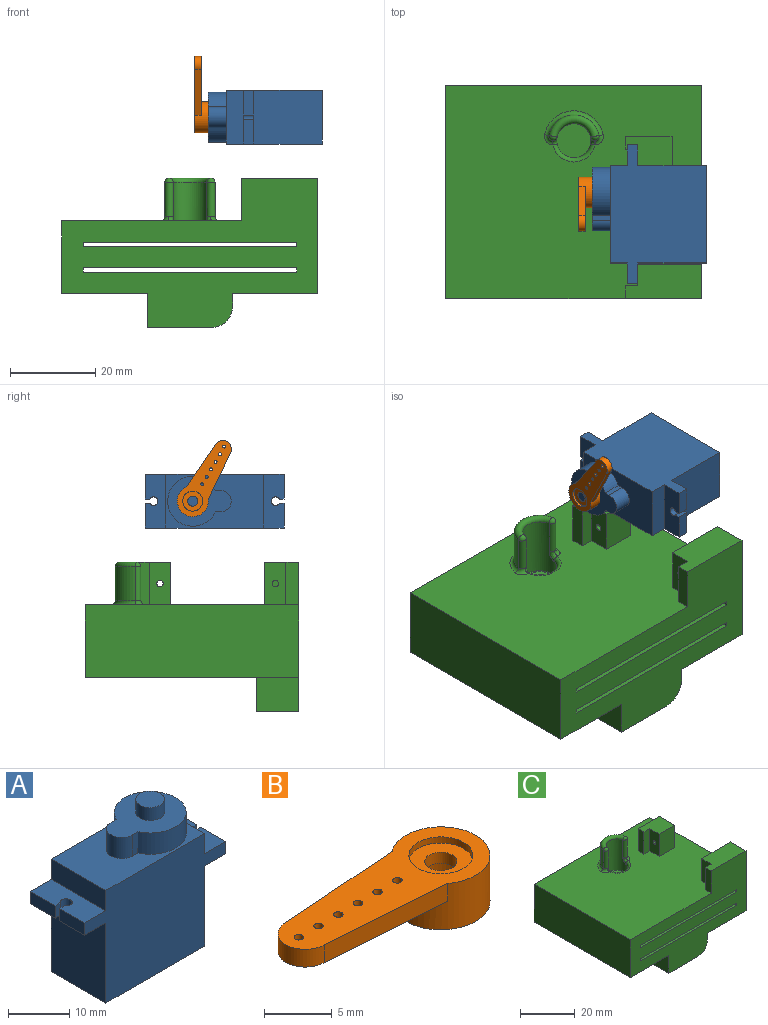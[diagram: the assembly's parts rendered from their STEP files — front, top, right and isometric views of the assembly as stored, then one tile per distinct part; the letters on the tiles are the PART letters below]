
ASSEMBLY  parts=3 mates=2
PART A: 29 faces, bbox 32.6x12.6x29.4 mm
  f0: plane 22.8x12.6mm, normal (0,0,1), area 164.9mm2, adj f3,f4,f5,f6,f22,f23,f24,f25
  f1: plane 16x12.6mm, normal (-1,0,0), area 201.6mm2, adj f4,f6,f7,f21
  f2: plane 16x12.6mm, normal (1,0,0), area 201.6mm2, adj f4,f6,f7,f14
  f3: plane 12.6x4.05mm, normal (1,0,0), area 51mm2, adj f0,f4,f6,f13
  f4: plane 32.6x22.5mm, normal (0,1,0), area 537mm2, adj f0,f1,f2,f3,f5,f7,f12,f13
  f5: plane 12.6x4.05mm, normal (-1,0,0), area 51mm2, adj f0,f4,f6,f20
  f6: plane 32.6x22.5mm, normal (0,-1,0), area 537mm2, adj f0,f1,f2,f3,f5,f7,f8,f13
  f7: plane 22.8x12.6mm, normal (0,0,-1), area 287.3mm2, adj f1,f2,f4,f6
  f8: plane 5.8x2.45mm, normal (1,0,0), area 14.2mm2, adj f6,f9,f13,f14
  f9: plane 2.45x1.13mm, normal (0,1,0), area 2.8mm2, adj f8,f10,f13,f14
  f10: cylinder r=1mm len=2.45mm, axis (0,0,-1), area 12.8mm2, adj f9,f11,f13,f14
  f11: plane 2.45x1.13mm, normal (0,-1,0), area 2.8mm2, adj f10,f12,f13,f14
  f12: plane 5.8x2.45mm, normal (1,0,0), area 14.2mm2, adj f4,f11,f13,f14
  f13: plane 12.6x4.9mm, normal (0,0,1), area 57.6mm2, adj f3,f4,f6,f8,f9,f10,f11,f12
  f14: plane 12.6x4.9mm, normal (0,0,-1), area 57.6mm2, adj f2,f4,f6,f8,f9,f10,f11,f12
  f15: plane 5.8x2.45mm, normal (-1,0,0), area 14.2mm2, adj f4,f16,f20,f21
  f16: plane 2.45x1.13mm, normal (0,-1,0), area 2.8mm2, adj f15,f17,f20,f21
  f17: cylinder r=1mm len=2.45mm, axis (0,0,-1), area 12.8mm2, adj f16,f18,f20,f21
  f18: plane 2.45x1.13mm, normal (0,1,0), area 2.8mm2, adj f17,f19,f20,f21
  f19: plane 5.8x2.45mm, normal (-1,0,0), area 14.2mm2, adj f6,f18,f20,f21
  f20: plane 12.6x4.9mm, normal (0,0,1), area 57.6mm2, adj f4,f5,f6,f15,f16,f17,f18,f19
  f21: plane 12.6x4.9mm, normal (0,0,-1), area 57.6mm2, adj f1,f4,f6,f15,f16,f17,f18,f19
  f22: plane 4.25x1.21mm, normal (0,1,0), area 5.1mm2, adj f0,f23,f25,f26
  f23: cylinder r=2.5mm len=5mm, axis (0,0,-1), area 33.4mm2, adj f0,f22,f24,f26
  f24: plane 4.25x1.21mm, normal (0,-1,0), area 5.1mm2, adj f0,f23,f25,f26
  f25: cylinder r=5.88mm len=11.75mm, axis (0,0,-1), area 134.9mm2, adj f0,f22,f24,f26
  f26: plane 14.9x11.75mm, normal (0,0,1), area 105.1mm2, adj f22,f23,f24,f25,f27
  f27: cylinder r=2.35mm len=4.7mm, axis (0,0,-1), area 38.4mm2, adj f26,f28
  f28: plane 4.7x4.7mm, normal (0,0,1), area 17.3mm2, adj f27
PART B: 18 faces, bbox 19.8x7.3x4.2 mm
  f0: cylinder r=2.35mm len=4.7mm, axis (0,0,-1), area 38.4mm2, adj f13,f15
  f1: cylinder r=3.62mm len=7.25mm, axis (0,0,-1), area 83.8mm2, adj f2,f9,f12,f13,f17
  f2: plane 11.95x1.6mm, normal (-0.08,1,0), area 19.2mm2, adj f1,f3,f12,f17
  f3: cylinder r=2mm len=4mm, axis (0,0,-1), area 10.1mm2, adj f2,f9,f12,f17
  f4: cylinder r=0.35mm len=1.6mm, axis (0,0,-1), area 3.5mm2, adj f12,f17
  f5: cylinder r=0.35mm len=1.6mm, axis (0,0,-1), area 3.5mm2, adj f12,f17
  f6: cylinder r=0.35mm len=1.6mm, axis (0,0,-1), area 3.5mm2, adj f12,f17
  f7: cylinder r=0.35mm len=1.6mm, axis (0,0,-1), area 3.5mm2, adj f12,f17
  f8: cylinder r=0.35mm len=1.6mm, axis (0,0,-1), area 3.5mm2, adj f12,f17
  f9: plane 11.95x1.6mm, normal (-0.08,-1,0), area 19.2mm2, adj f1,f3,f12,f17
  f10: cylinder r=2.35mm len=4.7mm, axis (0,0,-1), area 8.1mm2, adj f12,f14
  f11: cylinder r=0.35mm len=1.6mm, axis (0,0,-1), area 3.5mm2, adj f12,f17
  f12: plane 19.75x7.25mm, normal (0,0,1), area 80.6mm2, adj f1,f2,f3,f4,f5,f6,f7,f8
  f13: plane 7.25x7.25mm, normal (0,0,-1), area 23.9mm2, adj f0,f1
  f14: plane 4.7x4.7mm, normal (0,0,1), area 13mm2, adj f10,f16
  f15: plane 4.7x4.7mm, normal (0,0,-1), area 13mm2, adj f0,f16
  f16: cylinder r=1.18mm len=2.35mm, axis (0,0,-1), area 7.4mm2, adj f14,f15
  f17: plane 13.95x5.8mm, normal (0,0,-1), area 56.7mm2, adj f1,f2,f3,f4,f5,f6,f7,f8
PART C: 52 faces, bbox 60x50x35 mm
  f0: cylinder r=4mm len=14mm, axis (0,0,1), area 211.5mm2, adj f26,f34,f39,f40,f44,f45,f46
  f1: plane 60x17mm, normal (0,1,0), area 920mm2, adj f4,f5,f6,f7,f22,f23,f24,f25
  f2: plane 60x35mm, normal (0,-1,0), area 1254.6mm2, adj f4,f5,f6,f7,f11,f12,f22,f23
  f3: plane 10x8mm, normal (0,-1,0), area 80mm2, adj f4,f16,f17,f18
  f4: plane 60x50mm, normal (0,0,1), area 2679.8mm2, adj f1,f2,f3,f5,f6,f8,f9,f10
  f5: plane 50x27mm, normal (1,0,0), area 930mm2, adj f1,f2,f4,f7,f8,f12
  f6: plane 50x17mm, normal (-1,0,0), area 850mm2, adj f1,f2,f4,f7
  f7: plane 60x50mm, normal (0,0,-1), area 2800mm2, adj f1,f2,f5,f6,f47,f48,f49
  f8: plane 15x10mm, normal (0,1,0), area 150mm2, adj f4,f5,f9,f12
  f9: plane 10x5mm, normal (-1,0,0), area 48.2mm2, adj f4,f8,f10,f12,f20
  f10: plane 10x3mm, normal (0,1,0), area 30mm2, adj f4,f9,f11,f12
  f11: plane 10x3mm, normal (-1,0,0), area 30mm2, adj f2,f4,f10,f12
  f12: plane 18x8mm, normal (0,0,1), area 129mm2, adj f2,f5,f8,f9,f10,f11
  f13: plane 11x10mm, normal (0,1,0), area 110mm2, adj f4,f14,f17,f18
  f14: plane 10x3mm, normal (-1,0,0), area 30mm2, adj f4,f13,f15,f17
  f15: plane 10x3mm, normal (0,-1,0), area 30mm2, adj f4,f14,f16,f17
  f16: plane 10x5mm, normal (-1,0,0), area 48.2mm2, adj f3,f4,f15,f17,f19
  f17: plane 11x8mm, normal (0,0,1), area 73mm2, adj f3,f13,f14,f15,f16,f18
  f18: plane 10x8mm, normal (1,0,0), area 78.2mm2, adj f3,f4,f13,f17,f19
  f19: cylinder r=0.75mm len=8mm, axis (-1,0,0), area 37.7mm2, adj f16,f18
  f20: cylinder r=0.75mm len=8mm, axis (-1,0,0), area 37.7mm2, adj f9,f21
  f21: plane 1.5x1.5mm, normal (-1,0,0), area 1.8mm2, adj f20
  f22: plane 50x50mm, normal (0,0,-1), area 2500mm2, adj f1,f2,f23,f25
  f23: plane 50x1mm, normal (-1,0,0), area 50mm2, adj f1,f2,f22,f24
  f24: plane 50x50mm, normal (0,0,1), area 2500mm2, adj f1,f2,f23,f25
  f25: plane 50x1mm, normal (1,0,0), area 50mm2, adj f1,f2,f22,f24
  f26: plane 50x50mm, normal (0,0,-1), area 2449.7mm2, adj f0,f1,f2,f27,f29
  f27: plane 50x1mm, normal (-1,0,0), area 50mm2, adj f1,f2,f26,f28
  f28: plane 50x50mm, normal (0,0,1), area 2421.5mm2, adj f1,f2,f27,f29,f32
  f29: plane 50x1mm, normal (1,0,0), area 50mm2, adj f1,f2,f26,f28
  f30: plane 8x8mm, normal (0,0,1), area 50.3mm2, adj f31
  f31: cylinder r=4mm len=8mm, axis (0,0,1), area 50.3mm2, adj f30,f32
  f32: torus R=5mm, axis (0,0,-1), area 43.1mm2, adj f28,f31
  f33: cylinder r=6mm len=11.76mm, axis (0,0,-1), area 131.5mm2, adj f34,f37,f39,f40
  f34: torus R=5mm, axis (0,0,1), area 43mm2, adj f0,f33,f35,f36
  f35: sphere r=1mm, area 3.1mm2, adj f34,f39
  f36: sphere r=1mm, area 3.1mm2, adj f34,f40
  f37: torus R=7mm, axis (0,0,1), area 27.4mm2, adj f4,f33,f38,f41
  f38: torus R=2mm, axis (0,0,1), area 3.8mm2, adj f4,f37,f39,f42
  f39: cylinder r=1mm len=8mm, axis (0,0,-1), area 25.1mm2, adj f0,f33,f35,f38,f44
  f40: cylinder r=1mm len=8mm, axis (0,0,-1), area 25.1mm2, adj f0,f33,f36,f41,f45
  f41: torus R=2mm, axis (0,0,1), area 3.8mm2, adj f4,f37,f40,f43
  f42: cylinder r=1mm len=1mm, axis (1,0,0), area 0.1mm2, adj f38,f44
  f43: cylinder r=1mm len=1mm, axis (1,0,0), area 0.1mm2, adj f41,f45
  f44: bspline ~2.44x1.94mm, area 2.9mm2, adj f0,f39,f42,f46
  f45: bspline ~2.22x2.01mm, area 2.9mm2, adj f0,f40,f43,f46
  f46: torus R=5mm, axis (0,0,1), area 18.8mm2, adj f0,f4,f44,f45
  f47: plane 10x8mm, normal (-1,0,0), area 80mm2, adj f2,f7,f48,f50
  f48: plane 20x8mm, normal (0,1,0), area 154.6mm2, adj f7,f47,f49,f50,f51
  f49: plane 10x3mm, normal (1,0,0), area 30mm2, adj f2,f7,f48,f51
  f50: plane 15x10mm, normal (0,0,-1), area 150mm2, adj f2,f47,f48,f51
  f51: cylinder r=5mm len=10mm, axis (0,1,0), area 78.5mm2, adj f2,f48,f49,f50
PLACE A rot(axis=(-0.58,-0.58,0.58),120deg) t=(5.86,33.61,33.9)mm
PLACE B rot(axis=(-0.69,-0.19,0.69),158.9deg) t=(6.86,36.17,38.34)mm
PLACE C t=(-25.14,38.91,-7.4)mm
MATE revolute B.f16 <-> A.f27  axis (-1,0,0) through (-23.49,38.73,33.9)mm
MATE fastened A.f14 <-> C.f16  axis (1,0,0) through (-10.14,49.91,27.6)mm
